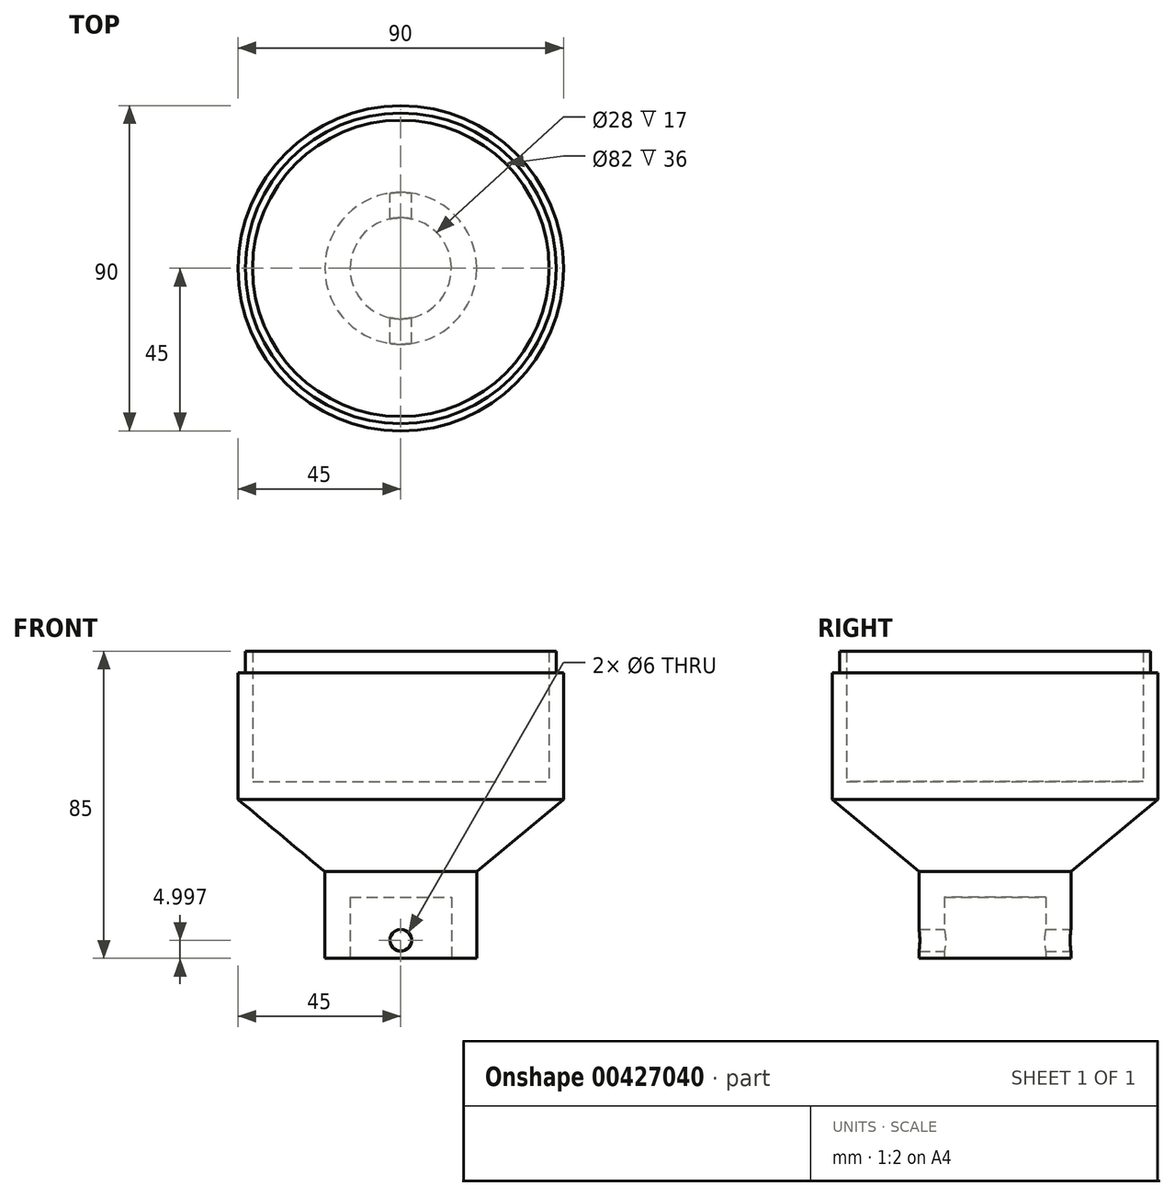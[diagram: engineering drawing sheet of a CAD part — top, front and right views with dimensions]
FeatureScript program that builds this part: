
annotation { "Feature Type Name" : "Feature", "Feature Type Description" : "" }
export const myFeature = defineFeature(function(context is Context, id is Id, definition is map)
    precondition{}
    {
        {
            var Q0;
            Q0=qCreatedBy(makeId("Front.planeOp"),FACE);
            var sketch = newSketch(context, id + "F0", { "sketchPlane" : qUnion([Q0])});
            skLineSegment(sketch, "E0", {"start": v(0, -97.36) * mm, "end": v(0, 38.15) * mm, "construction": true});
            skLineSegment(sketch, "E1", {"start": v(0, -29.6) * mm, "end": v(21, -29.6) * mm, "construction": true});
            skLineSegment(sketch, "E2", {"start": v(21, -53.6) * mm, "end": v(14, -53.6) * mm});
            skLineSegment(sketch, "E3", {"start": v(14, -53.6) * mm, "end": v(14, -36.6) * mm});
            skLineSegment(sketch, "E4", {"start": v(14, -36.6) * mm, "end": v(0, -36.6) * mm});
            skLineSegment(sketch, "E5", {"start": v(21, -53.6) * mm, "end": v(21, -29.6) * mm});
            skLineSegment(sketch, "E6", {"start": v(0, -9.6) * mm, "end": v(45, -9.6) * mm, "construction": true});
            skLineSegment(sketch, "E7", {"start": v(21, -29.6) * mm, "end": v(45, -9.6) * mm});
            skLineSegment(sketch, "E8", {"start": v(0, -29.6) * mm, "end": v(0, -9.6) * mm, "construction": true});
            skLineSegment(sketch, "E9", {"start": v(0, -36.6) * mm, "end": v(0, -29.6) * mm});
            skLineSegment(sketch, "E10", {"start": v(0, -9.6) * mm, "end": v(0, -4.6) * mm});
            skLineSegment(sketch, "E11", {"start": v(0, -9.6) * mm, "end": v(0, -29.6) * mm});
            skLineSegment(sketch, "E12", {"start": v(45, -9.6) * mm, "end": v(45, -4.6) * mm});
            skLineSegment(sketch, "E13", {"start": v(0, -4.6) * mm, "end": v(41, -4.6) * mm});
            skLineSegment(sketch, "E14", {"start": v(45, -4.6) * mm, "end": v(45, 25.4) * mm});
            skLineSegment(sketch, "E15", {"start": v(45, 25.4) * mm, "end": v(43, 25.4) * mm});
            skLineSegment(sketch, "E16", {"start": v(43, 25.4) * mm, "end": v(43, 31.4) * mm});
            skLineSegment(sketch, "E17", {"start": v(41, -4.6) * mm, "end": v(41, 31.4) * mm});
            skLineSegment(sketch, "E18", {"start": v(41, 31.4) * mm, "end": v(43, 31.4) * mm});
            skSolve(sketch);
        }
        {
            var Q0;
            Q0=makeQuery(id+"F0.imprint","IMPRINT",FACE,{"disambiguationData":[TD([[makeQuery(id+"F0.imprint","IMPRINT",EDGE,{"derivedFrom":sQuery(id+"F0.wireOp",EDGE,"E2")}),-1.0]])]});
            var Q1;
            Q1=sQuery(id+"F0.wireOp",EDGE,"E0");
            revolve(context, id + "F1", {"entities" : qUnion([Q0]), "axis" : qUnion([Q1]), "revolveType" : RevolveType.FULL});
        }
        {
            var Q0;
            Q0=qCreatedBy(makeId("Front.planeOp"),FACE);
            var sketch = newSketch(context, id + "F2", { "sketchPlane" : qUnion([Q0])});
            skLineSegment(sketch, "E19.0", {"start": v(21, -53.6) * mm, "end": v(-21, -53.6) * mm, "construction": true});
            skLineSegment(sketch, "E20", {"start": v(21, -53.6) * mm, "end": v(21, -43.6) * mm, "construction": true});
            skLineSegment(sketch, "E21", {"start": v(21, -43.6) * mm, "end": v(-21, -43.6) * mm, "construction": true});
            skLineSegment(sketch, "E22", {"start": v(-21, -43.6) * mm, "end": v(-21, -53.6) * mm, "construction": true});
            skLineSegment(sketch, "E23", {"start": v(0, -53.6) * mm, "end": v(0, -43.6) * mm, "construction": true});
            skCircle(sketch, "E24", {"center": v(0, -48.6) * mm, "radius": 3 * mm});
            skSolve(sketch);
        }
        {
            var Q0;
            Q0=makeQuery(id+"F2.imprint","IMPRINT",FACE,{"disambiguationData":[TD([[makeQuery(id+"F2.imprint","IMPRINT",EDGE,{"derivedFrom":sQuery(id+"F2.wireOp",EDGE,"E24")}),1.0]])]});
            var Q1;
            Q1=sQuery(id+"F2.wireOp",EDGE,"E24");
            extrude(context, id + "F3", {"entities" : qUnion([Q0]), "operationType" : NewBodyOperationType.REMOVE, "surfaceEntities" : qUnion([Q1]), "endBound" : BoundingType.SYMMETRIC, "depth" : 50 * mm});
        }
    });
